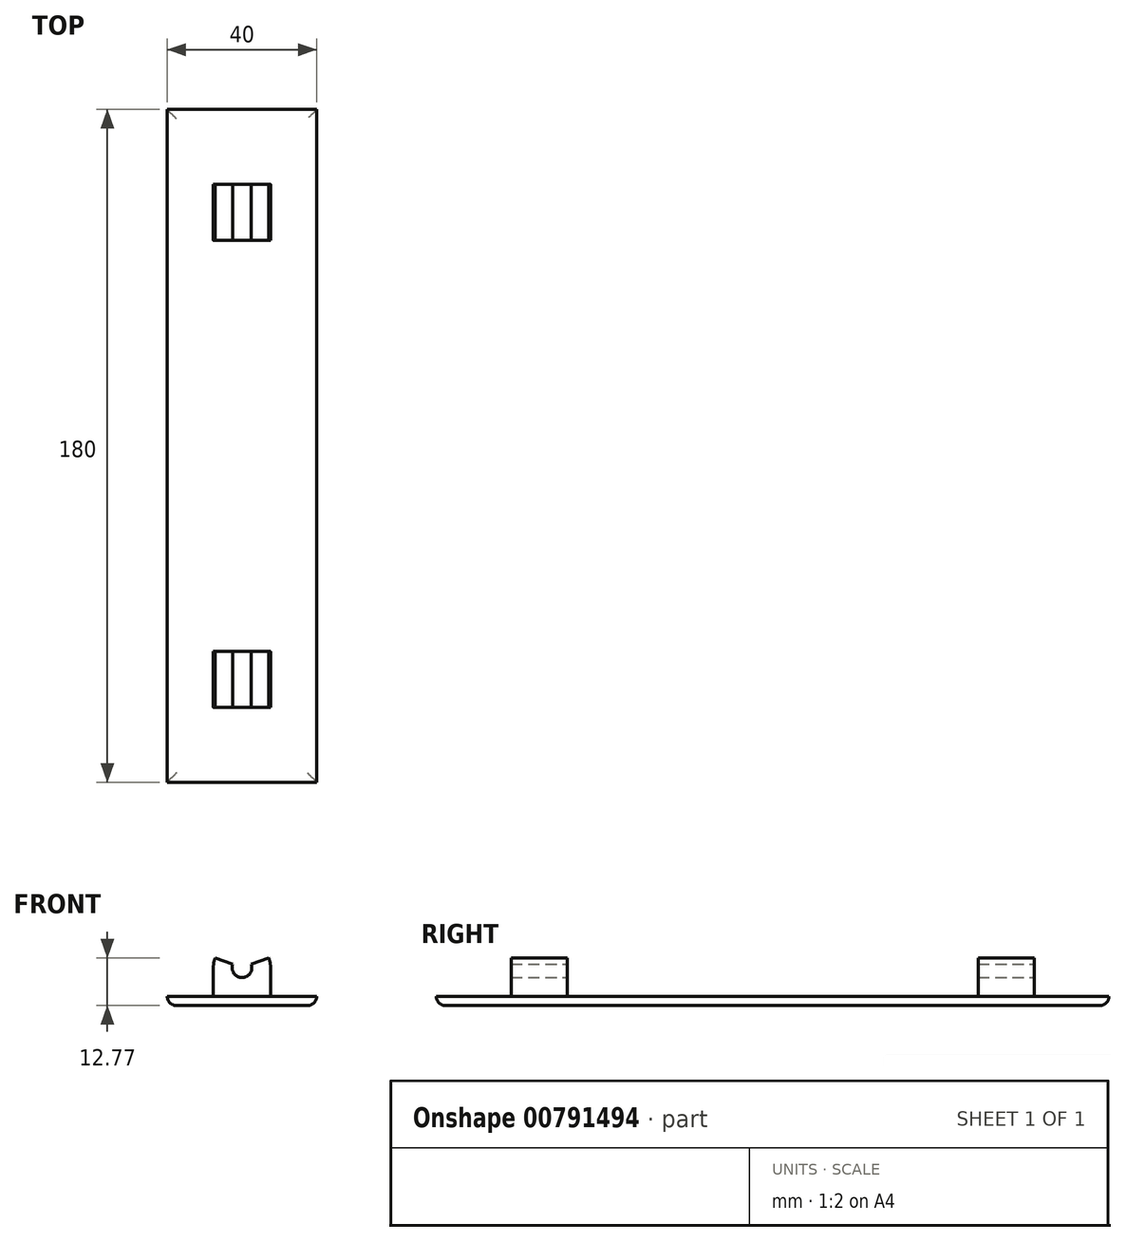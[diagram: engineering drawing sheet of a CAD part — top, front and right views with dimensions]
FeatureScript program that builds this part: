
annotation { "Feature Type Name" : "Feature", "Feature Type Description" : "" }
export const myFeature = defineFeature(function(context is Context, id is Id, definition is map)
    precondition{}
    {
        {
            var Q0;
            Q0=qCreatedBy(makeId("Front.planeOp"),FACE);
            var sketch = newSketch(context, id + "F0", { "sketchPlane" : qUnion([Q0])});
            skArc(sketch, "E0", {"start": v(-2.5, 0.9) * mm, "mid": v(0, -2.65) * mm, "end": v(2.5, 0.9) * mm});
            skArc(sketch, "E1.0", {"start": v(-7.19, 2.62) * mm, "mid": v(0, -7.65) * mm, "end": v(7.19, 2.62) * mm});
            skLineSegment(sketch, "E2", {"start": v(0, -7.65) * mm, "end": v(20, -7.65) * mm});
            skLineSegment(sketch, "E3", {"start": v(0, -7.65) * mm, "end": v(-20, -7.65) * mm});
            skLineSegment(sketch, "E4", {"start": v(-20, -7.65) * mm, "end": v(-20, -10.15) * mm});
            skLineSegment(sketch, "E5", {"start": v(-20, -10.15) * mm, "end": v(20, -10.15) * mm});
            skLineSegment(sketch, "E6", {"start": v(20, -10.15) * mm, "end": v(20, -7.65) * mm});
            skLineSegment(sketch, "E7", {"start": v(-7.65, 0) * mm, "end": v(-7.65, -7.65) * mm});
            skLineSegment(sketch, "E8", {"start": v(7.65, 0) * mm, "end": v(7.65, -7.65) * mm});
            skLineSegment(sketch, "E9", {"start": v(0, 0) * mm, "end": v(0, 9.39) * mm, "construction": true});
            skLineSegment(sketch, "E10", {"start": v(0, 0) * mm, "end": v(11.34, 4.13) * mm, "construction": true});
            skLineSegment(sketch, "E11.MirrorCS", {"start": v(0, 0) * mm, "end": v(-11.34, 4.13) * mm, "construction": true});
            skLineSegment(sketch, "E12", {"start": v(-2.5, 0.9) * mm, "end": v(-7.19, 2.62) * mm});
            skLineSegment(sketch, "E13", {"start": v(2.5, 0.9) * mm, "end": v(7.19, 2.62) * mm});
            skSolve(sketch);
        }
        {
            var Q0;
            Q0 = qSketchRegion(id + "F0", true);
            extrude(context, id + "F1", {"entities" : qUnion([Q0]), "depth" : 180 * mm, "offsetDistance" : 25 * mm});
        }
        {
            var Q0;
            Q0=makeQuery(id+"F1.opExtrude","SWEPT_FACE",FACE,{"disambiguationData":[OSD([sQuery(id+"F0.wireOp",EDGE,"E2")])]});
            var sketch = newSketch(context, id + "F2", { "sketchPlane" : qUnion([Q0])});
            skLineSegment(sketch, "E14", {"start": v(20, -160) * mm, "end": v(7.65, -160) * mm});
            skLineSegment(sketch, "E15", {"start": v(20, -145) * mm, "end": v(7.65, -145) * mm});
            skLineSegment(sketch, "E16", {"start": v(20, -35) * mm, "end": v(7.65, -35) * mm});
            skLineSegment(sketch, "E17", {"start": v(20, -20) * mm, "end": v(7.65, -20) * mm});
            skLineSegment(sketch, "E18", {"start": v(7.65, -160) * mm, "end": v(7.65, -145) * mm});
            skLineSegment(sketch, "E19", {"start": v(20, -160) * mm, "end": v(20, -145) * mm});
            skLineSegment(sketch, "E20", {"start": v(7.65, -35) * mm, "end": v(7.65, -20) * mm});
            skLineSegment(sketch, "E21", {"start": v(20, -35) * mm, "end": v(20, -20) * mm});
            skLineSegment(sketch, "E22", {"start": v(9.65, -35) * mm, "end": v(9.65, -20) * mm});
            skLineSegment(sketch, "E23", {"start": v(9.65, -160) * mm, "end": v(9.65, -145) * mm});
            skLineSegment(sketch, "E24.0", {"start": v(7.65, -180) * mm, "end": v(20, -180) * mm});
            skLineSegment(sketch, "E24.1", {"start": v(7.65, -180) * mm, "end": v(7.65, 0) * mm});
            skLineSegment(sketch, "E24.2", {"start": v(7.65, 0) * mm, "end": v(20, 0) * mm});
            skLineSegment(sketch, "E25", {"start": v(9.65, -160) * mm, "end": v(9.65, -180) * mm});
            skLineSegment(sketch, "E26", {"start": v(9.65, -145) * mm, "end": v(9.65, -35) * mm});
            skLineSegment(sketch, "E27", {"start": v(9.65, -20) * mm, "end": v(9.65, 0) * mm});
            skSolve(sketch);
        }
        {
            var Q0;
            {var subQ3=sQuery(id+"F2.wireOp",EDGE,"E25");Q0=makeQuery(id+"F2.imprint","IMPRINT",FACE,{"disambiguationData":[TD([[makeQuery(id+"F2.imprint","IMPRINT",EDGE,{"derivedFrom":subQ3}),1.0]])]});}
            var Q1;
            {var subQ3=sQuery(id+"F2.wireOp",EDGE,"E26");Q1=makeQuery(id+"F2.imprint","IMPRINT",FACE,{"disambiguationData":[TD([[makeQuery(id+"F2.imprint","IMPRINT",EDGE,{"derivedFrom":subQ3}),-1.0]])]});}
            var Q2;
            {var subQ3=sQuery(id+"F2.wireOp",EDGE,"E27");Q2=makeQuery(id+"F2.imprint","IMPRINT",FACE,{"disambiguationData":[TD([[makeQuery(id+"F2.imprint","IMPRINT",EDGE,{"derivedFrom":subQ3}),-1.0]])]});}
            extrude(context, id + "F3", {"entities" : qUnion([Q0, Q1, Q2]), "operationType" : NewBodyOperationType.ADD, "depth" : 25 * mm, "offsetDistance" : 25 * mm});
        }
        {
            var Q0;
            Q0=makeQuery(id+"F3.opExtrude","SWEPT_FACE",FACE,{"disambiguationData":[OSD([sQuery(id+"F2.wireOp",EDGE,"E27")])]});
            var Q1;
            Q1=makeQuery(id+"F3.opExtrude","SWEPT_FACE",FACE,{"disambiguationData":[OSD([sQuery(id+"F2.wireOp",EDGE,"E26")])]});
            var Q2;
            Q2=makeQuery(id+"F3.opExtrude","SWEPT_FACE",FACE,{"disambiguationData":[OSD([sQuery(id+"F2.wireOp",EDGE,"E25")])]});
            extrude(context, id + "F4", {"entities" : qUnion([Q0, Q1, Q2]), "operationType" : NewBodyOperationType.REMOVE, "depth" : 25 * mm, "offsetDistance" : 25 * mm});
        }
        {
            var Q0;
            Q0=makeQuery(id+"F3.opExtrude","SWEPT_FACE",FACE,{"disambiguationData":[OSD([sQuery(id+"F2.wireOp",EDGE,"E27")])]});
            var Q1;
            Q1=makeQuery(id+"F3.opExtrude","SWEPT_FACE",FACE,{"disambiguationData":[OSD([sQuery(id+"F2.wireOp",EDGE,"E26")])]});
            var Q2;
            Q2=makeQuery(id+"F3.opExtrude","SWEPT_FACE",FACE,{"disambiguationData":[OSD([sQuery(id+"F2.wireOp",EDGE,"E25")])]});
            extrude(context, id + "F5", {"entities" : qUnion([Q0, Q1, Q2]), "operationType" : NewBodyOperationType.REMOVE, "oppositeDirection" : true, "depth" : 25 * mm, "offsetDistance" : 25 * mm});
        }
        {
            var Q0;
            Q0=makeQuery(id+"F1.opExtrude","SWEPT_EDGE",EDGE,{"disambiguationData":[OSD([sQuery(id+"F0.wireOp",EDGE,"E4"),sQuery(id+"F0.wireOp",EDGE,"E5")])]});
            var Q1;
            Q1=makeQuery(id+"F1.opExtrude","CAP_EDGE",EDGE,{"disambiguationData":[OSD([sQuery(id+"F0.wireOp",EDGE,"E5")])],"isStart":false});
            var Q2;
            Q2=makeQuery(id+"F1.opExtrude","SWEPT_EDGE",EDGE,{"disambiguationData":[OSD([sQuery(id+"F0.wireOp",EDGE,"E5"),sQuery(id+"F0.wireOp",EDGE,"E6")])]});
            var Q3;
            Q3=makeQuery(id+"F1.opExtrude","CAP_EDGE",EDGE,{"disambiguationData":[OSD([sQuery(id+"F0.wireOp",EDGE,"E5")])],"isStart":true});
            fillet(context, id + "F6", {"entities" : qUnion([Q0, Q1, Q2, Q3]), "radius" : 2.5 * mm, "tangentPropagation" : true, "allowEdgeOverflow" : false});
        }
    });
